# Revit family: BasinMixer-Countertop-ForBowls-Vitra-RootSeries-A42732
name_source: partatom
category: Plumbing Fixtures
revit_build: Autodesk Revit 2017 (Build: 20160225_1515(x64)
units: mm (PartAtom-declared; Revit-internal decimal feet)

## family parameters
Cut with Voids When Loaded = No
Host = Face
OmniClass Number = 23.45.55.17
OmniClass Title = Mixing Faucets
Part Type = Normal
Room Calculation Point = No
Round Connector Dimension = Use Diameter
Shared = Yes

## types (10) — shared parameters
BIMobject category = Taps & Mixers
CW Connection = Yes
Connection Diameter (mm) = 10 mm  [stored 0.0328084 ft]
Default Elevation = 850 mm  [stored 2.78871 ft]
Description = Root Basin Mixer - For Bowls
Design country = Turkey
Flow Rate(L/min. - 3 bar) = 5 L/min.
HW Connection = Yes
Hot Water Supply (max.) = 80 °C
Hot Water temperature, factory set to = 38 °C
IFC Classification = Sanitary Terminal
Main Material = Brass
Manufacturer = Vitra
Manufacturer name = Vitra
Masterformat 2014 Code = 22 40 00
Masterformat 2014 Description = Plumbing Fixtures
Min. flow pressure of = 0.5 bar
Mounting type = Countertop
NBS Referans Code = 45-35-70/371
NBS Referans Description = Water supply fittings for wash basins and troughs
Nominal Depth (mm) = 160 mm  [stored 0.524934 ft]
Nominal Height (mm) = 185 mm  [stored 0.606955 ft]
Nominal Width (mm) = 50 mm  [stored 0.164042 ft]
Number Of Connections = 2
OmniClass Code = 23.45.55.17
OmniClass Description = Mixing Faucets
Product Type = Basin Mixer
Product certification = https://www.vitraglobal.com
Product family = Root
Product group = Root Basin Mixer
Range of Hot Water Supply = 5 - 65 °C
Range of flow pressure = 1 - 5 bar
Test Pressure = 16 bar
URL = https://vitraglobal.com
Uniclass 1.4 Code = L725111
Uniclass 1.4 Description = Mixer taps
Uniclass 2.0 Code = Pr_40_30_96_98
Uniclass 2.0 Description = Washbasin Tap
Uniclass 2015 Code = Pr_40_20_87_98
Uniclass 2015 Name = Washbasin Tap
Uniformat II Code = 22 40 00
Uniformat II Description = Plumbing Fixture
Vent Connection = No
Warranty Period (Year) = 10 Years
Waste Connection = No
Weight Net (kg) = 2
Youtube = https://www.youtube.com

## per-type parameters (varying)
| type | Article No. (default) | Brand | Coating Material | Color | Model | Product Properties | Product SKU | Product url | Technical description |
| BasinMixer-Countertop-ForBowls-Vitra-RootSeries-A42732 | A42732 | Artema | Chrome (Metal) | Chrome | A42732 |  | A42732 | https://www.vitra.com.tr | https://www.vitra.com.tr |
| BasinMixer-Countertop-ForBowls-Vitra-RootSeries-A42732ENR | A42732ENR | Artema | Chrome (Metal) | Chrome | A42732ENR | Energy Saving - Blueco | A42732ENR | https://www.vitra.com.tr | https://www.vitra.com.tr |
| BasinMixer-Countertop-ForBowls-Vitra-RootSeries-A42732EXP | A42732EXP | VitrA | Chrome (Metal) | Chrome | A42732EXP |  | A42732EXP | https://www.vitraglobal.com | https://www.vitraglobal.com |
| BasinMixer-Countertop-ForBowls-Vitra-RootSeries-A42732ENG | A42732ENG | VitrA | Chrome (Metal) | Chrome | A42732ENG | Energy Saving - Blueco | A42732ENG | https://www.vitraglobal.com | https://www.vitraglobal.com |
| BasinMixer-Countertop-ForBowls-Vitra-RootSeries-A4273223EXP | A4273223EXP | VitrA | Gold (Metal) | Gold | A4273223EXP |  | A4273223EXP | https://www.vitraglobal.com | https://www.vitraglobal.com |
| BasinMixer-Countertop-ForBowls-Vitra-RootSeries-A4273223ENG | A4273223ENG | VitrA | Gold (Metal) | Gold | A4273223ENG | Energy Saving - Blueco | A4273223ENG | https://www.vitraglobal.com | https://www.vitraglobal.com |
| BasinMixer-Countertop-ForBowls-Vitra-RootSeries-A4273226EXP | A4273226EXP | VitrA | Copper (Metal) | Copper | A4273226EXP |  | A4273226EXP | https://www.vitraglobal.com | https://www.vitraglobal.com |
| BasinMixer-Countertop-ForBowls-Vitra-RootSeries-A4273226ENG | A4273226ENG | VitrA | Copper (Metal) | Copper | A4273226ENG | Energy Saving - Blueco | A4273226ENG | https://www.vitraglobal.com | https://www.vitraglobal.com |
| BasinMixer-Countertop-ForBowls-Vitra-RootSeries-A4273234EXP | A4273234EXP | VitrA | Gold (Metal) | Gold | A4273234EXP |  | A4273234EXP | https://www.vitraglobal.com | https://www.vitraglobal.com |
| BasinMixer-Countertop-ForBowls-Vitra-RootSeries-A4273234ENG | A4273234ENG | VitrA | Gold (Metal) | Gold | A4273234ENG | Energy Saving - Blueco | A4273234ENG | https://www.vitraglobal.com | https://www.vitraglobal.com |

note: [stored X ft] marks values corroborated as IEEE doubles in the binary element streams (Revit-internal decimal feet)

## geometry (parser evidence)
native form markers: Sweep x2
no freeform markers — native parametric forms only
